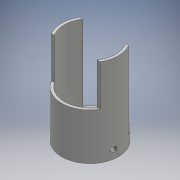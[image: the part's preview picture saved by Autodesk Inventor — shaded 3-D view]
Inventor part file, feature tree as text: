
AUTODESK INVENTOR PART (.ipt)
format: ipt  version: 2016 (Build 200138000, 138)  size: 170,496 bytes
history: native  units: mm
features: extrude x8, sketch x8, other x6
ambient origin geometry x8: Origin, YZ Plane, XZ Plane, XY Plane, X Axis, Y Axis, Z Axis, Center Point
bodies: Body1 (feature_tree)
feature tree (22):
  other  "ソリッド1"
  extrude  "押し出し1"  Depth=100.0mm
  sketch  "スケッチ2"
  other  "作業平面1"
  other  "作業平面2"
  other  "作業平面3"
  other  "作業平面4"
  extrude  "押し出し3"  Depth=110.0mm
  extrude  "押し出し4"  TaperAngle=30.0deg  [1 undecoded]
  extrude  "押し出し5"  TaperAngle=150.0deg  [1 undecoded]
  extrude  "押し出し6"  Depth=20.0mm TaperAngle=0.0deg
  other  "作業平面5"
  extrude  "押し出し9"  TaperAngle=30.0deg  [1 undecoded]
  extrude  "押し出し10"  TaperAngle=150.0deg  [1 undecoded]
  extrude  "押し出し11"  Depth=55.0mm
  sketch  "スケッチ1"
  sketch  "スケッチ3"
  sketch  "スケッチ4"
  sketch  "スケッチ5"
  sketch  "スケッチ6"
  sketch  "スケッチ8"
  sketch  "スケッチ9"
note: 4 required parameter values undecoded (feature->parameter linkage not recoverable at this tier; creation-order binding heuristic only, values carry confidence <= 0.55)
